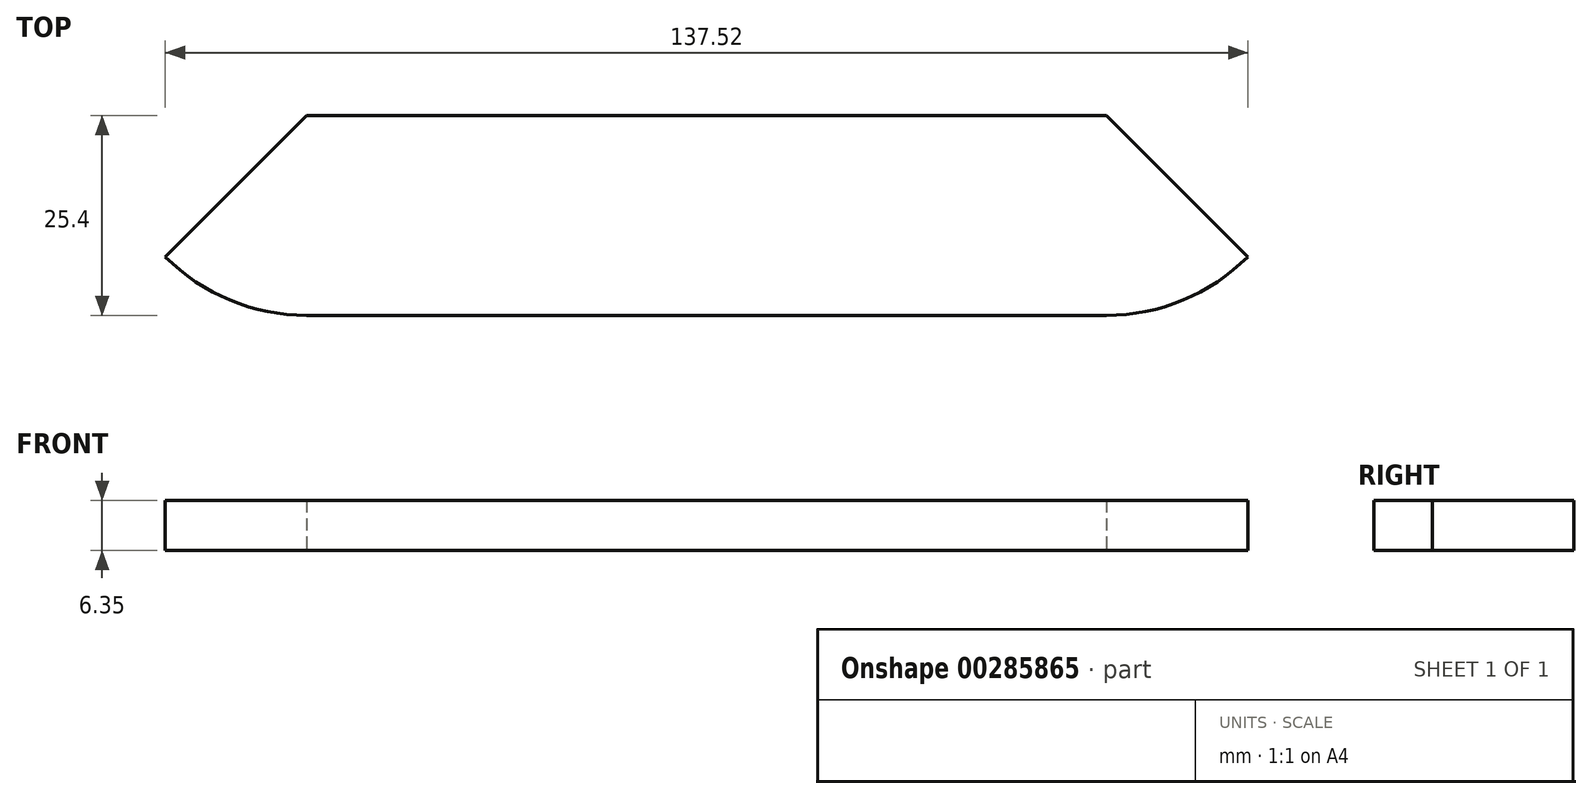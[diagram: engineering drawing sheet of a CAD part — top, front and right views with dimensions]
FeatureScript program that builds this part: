
annotation { "Feature Type Name" : "Feature", "Feature Type Description" : "" }
export const myFeature = defineFeature(function(context is Context, id is Id, definition is map)
    precondition{}
    {
        {
            var Q0;
            Q0=qCreatedBy(makeId("Top.planeOp"),FACE);
            var sketch = newSketch(context, id + "F0", { "sketchPlane" : qUnion([Q0])});
            skLineSegment(sketch, "E0.bottom", {"start": v(-25.4, 0) * mm, "end": v(-127, 0) * mm});
            skLineSegment(sketch, "E0.top", {"start": v(-25.4, -25.4) * mm, "end": v(-127, -25.4) * mm});
            skLineSegment(sketch, "E0.left", {"start": v(0, 0) * mm, "end": v(0, 0) * mm});
            skLineSegment(sketch, "E0.right", {"start": v(-152.4, 0) * mm, "end": v(-152.4, 0) * mm});
            skPoint(sketch, "E1.visualSharp", {"position": v(0, -25.4) * mm});
            skArc(sketch, "E1.filletArc", {"start": v(-25.4, -25.4) * mm, "mid": v(-15.68, -23.47) * mm, "end": v(-7.44, -17.96) * mm});
            skPoint(sketch, "E2.visualSharp", {"position": v(-152.4, -25.4) * mm});
            skArc(sketch, "E2.filletArc", {"start": v(-144.96, -17.96) * mm, "mid": v(-136.72, -23.47) * mm, "end": v(-127, -25.4) * mm});
            skLineSegment(sketch, "E3", {"start": v(-25.4, 0) * mm, "end": v(-7.44, -17.96) * mm});
            skLineSegment(sketch, "E4", {"start": v(-127, 0) * mm, "end": v(-144.96, -17.96) * mm});
            skSolve(sketch);
        }
        {
            var Q0;
            Q0=makeQuery(id+"F0.imprint","IMPRINT",FACE,{"disambiguationData":[TD([[makeQuery(id+"F0.imprint","IMPRINT",EDGE,{"derivedFrom":sQuery(id+"F0.wireOp",EDGE,"E0.bottom")}),1.0]])]});
            extrude(context, id + "F1", {"entities" : qUnion([Q0]), "depth" : 6.35 * mm});
        }
    });
